# Revit family: Haworth_Pergola_Ceiling_Slat_Radial
name_source: partatom
category: Furniture Systems
revit_build: Autodesk Revit 2018 (Build: 20170223_1515(x64)
units: mm (PartAtom-declared; Revit-internal decimal feet)

## family parameters
Always vertical = Yes
Cut with Voids When Loaded = No
OmniClass Number = 23.40.70.14.64.21
OmniClass Title = Systems Furniture
Part Type = Normal
Room Calculation Point = No
Round Connector Dimension = Use Diameter
Shared = No
Work Plane-Based = No

## types (2) — shared parameters
12in Slats = Yes
Actual Depth = 72 "
Actual Height = 3.63 "
Actual Mounting Height = 92.37 "
Actual Width = 144 "
Assembly Code = E2020200
Ceiling Slat Spacing = 6 "
Description = Haworth - Pergola Ceiling - Slat - Radial
Manufacturer = Haworth
Max. Depth = 144 "
Max. Height = 96 "
Max. Width = 144 "
Min. Depth = 48 "
Min. Height = 96 "
Min. Width = 48 "
Model = Haworth Pergola
Revision Number = 1
Size = Verify Final Dim. w/ Haworth
Slat 1 Width = 68.976 "
Slat 2 Width = 68.543 "
Slat 3 Width = 67.622 "
Slat 4 Width = 66.29 "
Slat 5 Width = 64.267 "
Slat 6 Width = 61.623 "
Slat 7 Width = 58.202 "
Slat 8 Width = 54.036 "
Standard Radius = 144 in.
Sustainability Info = http://www.haworth.com
Top Trim Width = 0.5 "
Trim Finish = Haworth _ Paint _ Undecided _ Pergola
URL = http://www.haworth.com
URL - Product = https://www.haworth.com
Warranty = http://www.haworth.com

## per-type parameters (varying)
| type | 12ft Full Round | 12ft Half Round | Ceiling Slat Offset | Full Round Slats | Slat 10 Width | Slat 11 Width | Slat 12 Width | Slat 9 Width | Slat Count |
| 144w - Full Round | Yes | No | 3 " | Yes | 41.911 " | 32.443 " | 17.818 " | 48.734 " | 11 |
| 144w - Half Round | No | Yes | 5 " | No | 44.446 " | 36.22 " | 24.09 " | 50.686 " | 10 |

## geometry (parser evidence)
native form markers: Sweep x5
no freeform markers — native parametric forms only
